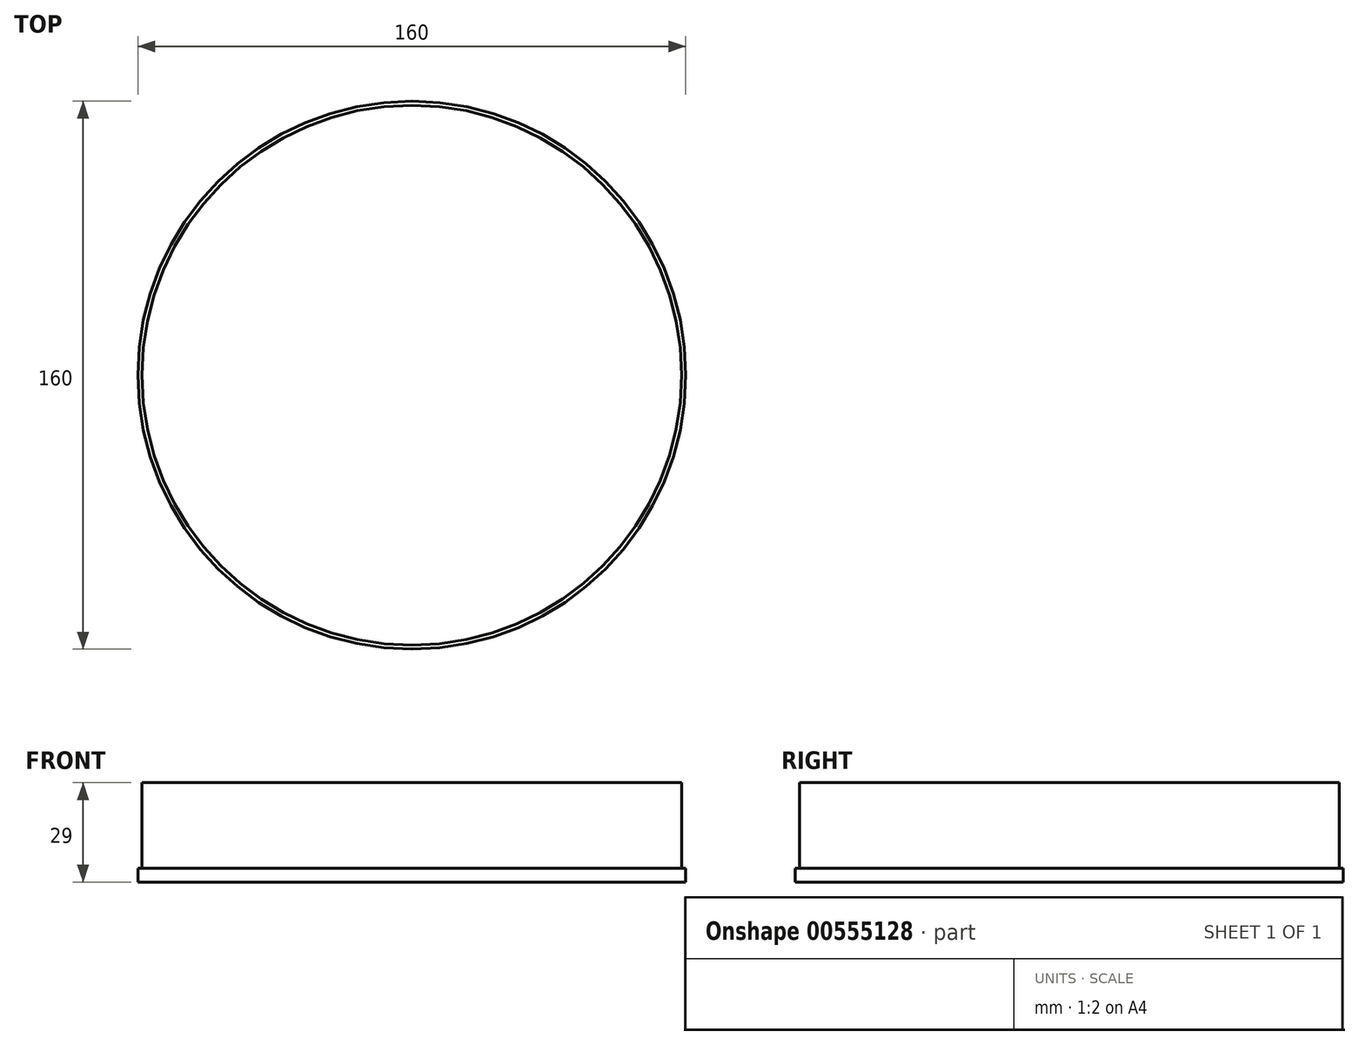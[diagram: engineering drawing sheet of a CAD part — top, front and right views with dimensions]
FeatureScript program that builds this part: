
annotation { "Feature Type Name" : "Feature", "Feature Type Description" : "" }
export const myFeature = defineFeature(function(context is Context, id is Id, definition is map)
    precondition{}
    {
        {
            var Q0;
            Q0=qCreatedBy(makeId("Top.planeOp"),FACE);
            var sketch = newSketch(context, id + "F0", { "sketchPlane" : qUnion([Q0])});
            skCircle(sketch, "E0", {"center": v(0, 0) * mm, "radius": 80 * mm});
            skSolve(sketch);
        }
        {
            var Q0;
            Q0=makeQuery(id+"F0.imprint","IMPRINT",FACE,{"disambiguationData":[TD([[makeQuery(id+"F0.imprint","IMPRINT",EDGE,{"derivedFrom":sQuery(id+"F0.wireOp",EDGE,"E0")}),1.0]])]});
            extrude(context, id + "F1", {"entities" : qUnion([Q0]), "depth" : 3 * mm, "offsetDistance" : 25 * mm});
        }
        {
            var Q0;
            Q0=makeQuery(id+"F1.opExtrude","CAP_FACE",FACE,{"disambiguationData":[OSD([sQuery(id+"F0.wireOp",EDGE,"E0")])],"isStart":false});
            var sketch = newSketch(context, id + "F2", { "sketchPlane" : qUnion([Q0])});
            skCircle(sketch, "E1.0", {"center": v(0, 0) * mm, "radius": 78.8 * mm});
            skSolve(sketch);
        }
        {
            var Q0;
            Q0=makeQuery(id+"F2.imprint","IMPRINT",FACE,{"disambiguationData":[TD([[makeQuery(id+"F2.imprint","IMPRINT",EDGE,{"derivedFrom":sQuery(id+"F2.wireOp",EDGE,"E1.0")}),1.0]])]});
            extrude(context, id + "F3", {"entities" : qUnion([Q0]), "operationType" : NewBodyOperationType.ADD, "depth" : 25 * mm, "offsetDistance" : 25 * mm});
        }
        {
            var Q0;
            Q0=makeQuery(id+"F1.opExtrude","CAP_FACE",FACE,{"disambiguationData":[OSD([sQuery(id+"F0.wireOp",EDGE,"E0")])],"isStart":true});
            extrude(context, id + "F4", {"entities" : qUnion([Q0]), "operationType" : NewBodyOperationType.ADD, "depth" : 1 * mm, "offsetDistance" : 25 * mm});
        }
    });
